# Revit family: Rax 200 U19 - Generic
name_source: partatom
category: Lighting Fixtures
revit_build: Autodesk Revit Architecture 2014 (Build: 20140709_2115(x64)
units: mm (PartAtom-declared; Revit-internal decimal feet)

## types (2) — shared parameters
Apparent Load = 240 VA
Clearance Zones = Yes
Diameter 1 = 223 mm
Height 1 = 160 mm
Light Source Definition (family) = Circle+HemiSpherical
OmniClass Number = 23.80.70.11
OmniClass Title = Luminaries for Internal Lighting

## per-type parameters (varying)
- Standard: Frame=<By Category>; Transformer Length=0 mm
- Rax 200 U19: ArticleNumber=See URL hyperlink; AssetType=Moveable/Fixed; BIMObjectName=Rax 200 U19.rfa; BSAB 96=SNB.2; BallastsCELMAEnergyEfficiencyIndex=Class A1/A2; CCSClassCode=UAC; CCSClassName=Belysningsarmatur; CCSTopnode=L; Colour=White, black, galvanized steel; ControlGearPosition=Integrated; Description=70-80-35 General Lighting Systems; DocumentReference=See URL hyperlink; Documentation=See URL hyperlink; Finish=Powder coated; Frame=Riegens_Aluminum_powder coated white gloss 25; HasProtectiveEarth=TRUE; IP_Code=IP20; IfcExportAs=IfcLightFixtureType'; IfcExportType=NOTDEFINED'; InsulationStandardClass=Class 1; InternalFuse=Only required in emergency versions; LampColourRenderingIndex=Ra>80 / Ra>90; LampRating=15W / 21W / 29W; LampType=LED; LightFixtureMountingType=Recessed; LightFixturePlacingType=Ceiling; LightSource=LED 3000K / 4000K; LuminairePowerFactor=>0,9; LuminaireType=Recessed Direct LED Luminaire; Manufacturer=Riegens A/S; ManufacturerURL=www.riegens.com; Material=Galvanized steel, aluminium and flame retardant PC; Model=Rax 200 U19; ModelReference=Rax 200 U19; NominalVoltage=220-240V; Optic=Satin-matt reflector; PhaseReference=IEC recommendations; PhotometricPerformance=In accordance with BS EN 13032-1; ProductInformation=http://riegens.co.uk; Shape=Circle; Size=Ø200 mm; TotalWattage=Max. 17W / 23W / 31W; Transformer Length=230 mm; URL=http://riegens.co.uk; Uniclass 1.4=JY73; Uniclass2=Pr_70_70_49_43 Light-Emitting Diode (LED) Luminaires; Version=v.1.0

## geometry (parser evidence)
native form markers: Blend x87, Sweep x4
no freeform markers — native parametric forms only
